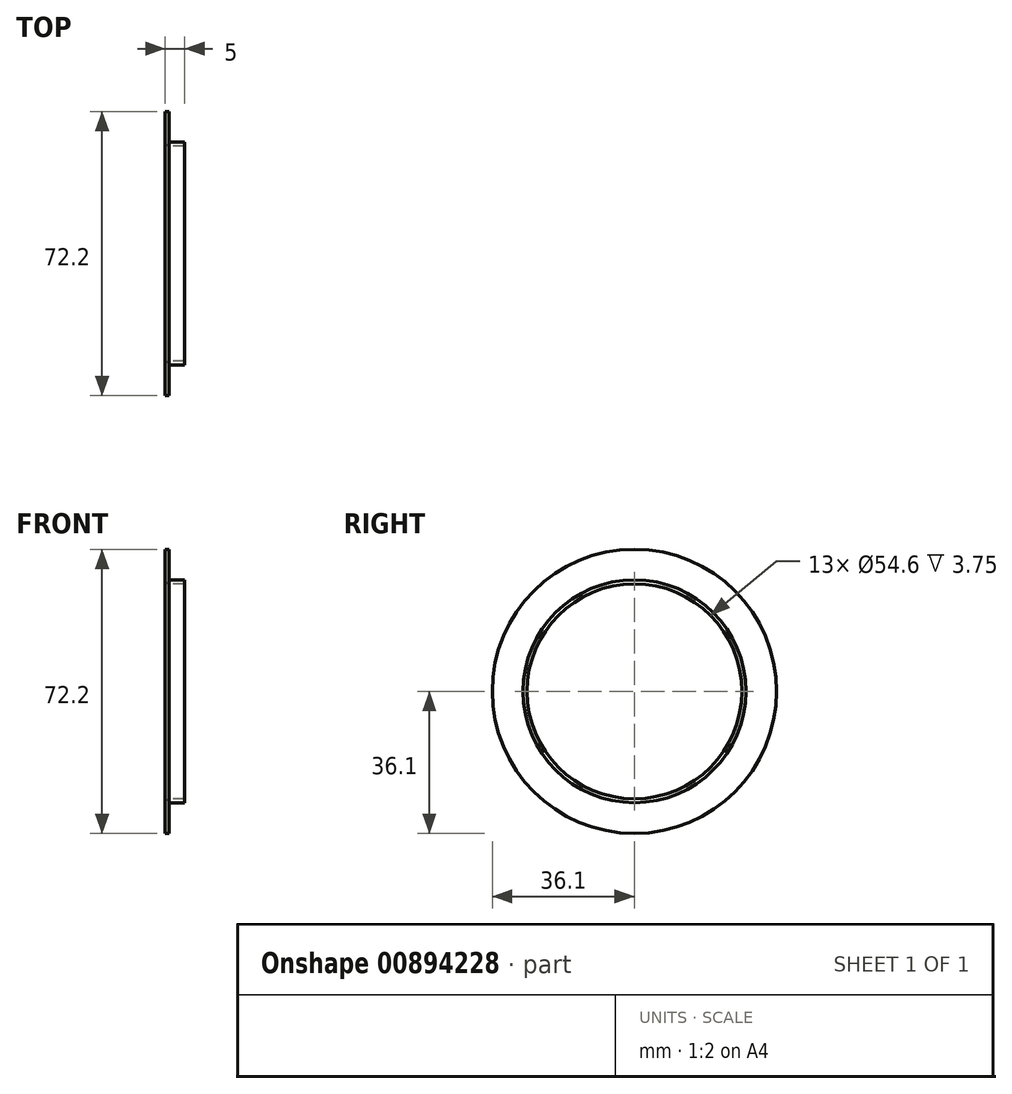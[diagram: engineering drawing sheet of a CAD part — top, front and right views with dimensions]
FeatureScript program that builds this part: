
annotation { "Feature Type Name" : "Feature", "Feature Type Description" : "" }
export const myFeature = defineFeature(function(context is Context, id is Id, definition is map)
    precondition{}
    {
        {
            var Q0;
            Q0=qCreatedBy(makeId("Front.planeOp"),FACE);
            var sketch = newSketch(context, id + "F0", { "sketchPlane" : qUnion([Q0])});
            skLineSegment(sketch, "E0", {"start": v(0, 28.55) * mm, "end": v(0, 36.1) * mm});
            skLineSegment(sketch, "E1", {"start": v(0, 36.1) * mm, "end": v(1, 36.1) * mm});
            skLineSegment(sketch, "E2", {"start": v(1, 36.1) * mm, "end": v(1, 28.55) * mm});
            skLineSegment(sketch, "E3", {"start": v(1.25, 28.3) * mm, "end": v(5, 28.3) * mm});
            skLineSegment(sketch, "E4", {"start": v(5, 28.3) * mm, "end": v(5, 27.3) * mm});
            skLineSegment(sketch, "E5", {"start": v(5, 27.3) * mm, "end": v(1.25, 27.3) * mm});
            skLineSegment(sketch, "E6", {"start": v(0, 0) * mm, "end": v(5, 0) * mm, "construction": true});
            skPoint(sketch, "E7.visualSharp", {"position": v(1, 28.3) * mm});
            skArc(sketch, "E7.filletArc", {"start": v(1, 28.55) * mm, "mid": v(1.07, 28.37) * mm, "end": v(1.25, 28.3) * mm});
            skPoint(sketch, "E8.visualSharp", {"position": v(0, 27.3) * mm});
            skArc(sketch, "E8.filletArc", {"start": v(0, 28.55) * mm, "mid": v(0.37, 27.67) * mm, "end": v(1.25, 27.3) * mm});
            skSolve(sketch);
        }
        {
            var Q0;
            Q0=qSketchRegion(id+"F0",true);
            var Q1;
            Q1=sQuery(id+"F0.wireOp",EDGE,"E6");
            revolve(context, id + "F1", {"surfaceOperationType" : NewSurfaceOperationType.NEW, "entities" : qUnion([Q0]), "axis" : qUnion([Q1]), "revolveType" : RevolveType.FULL});
        }
    });
